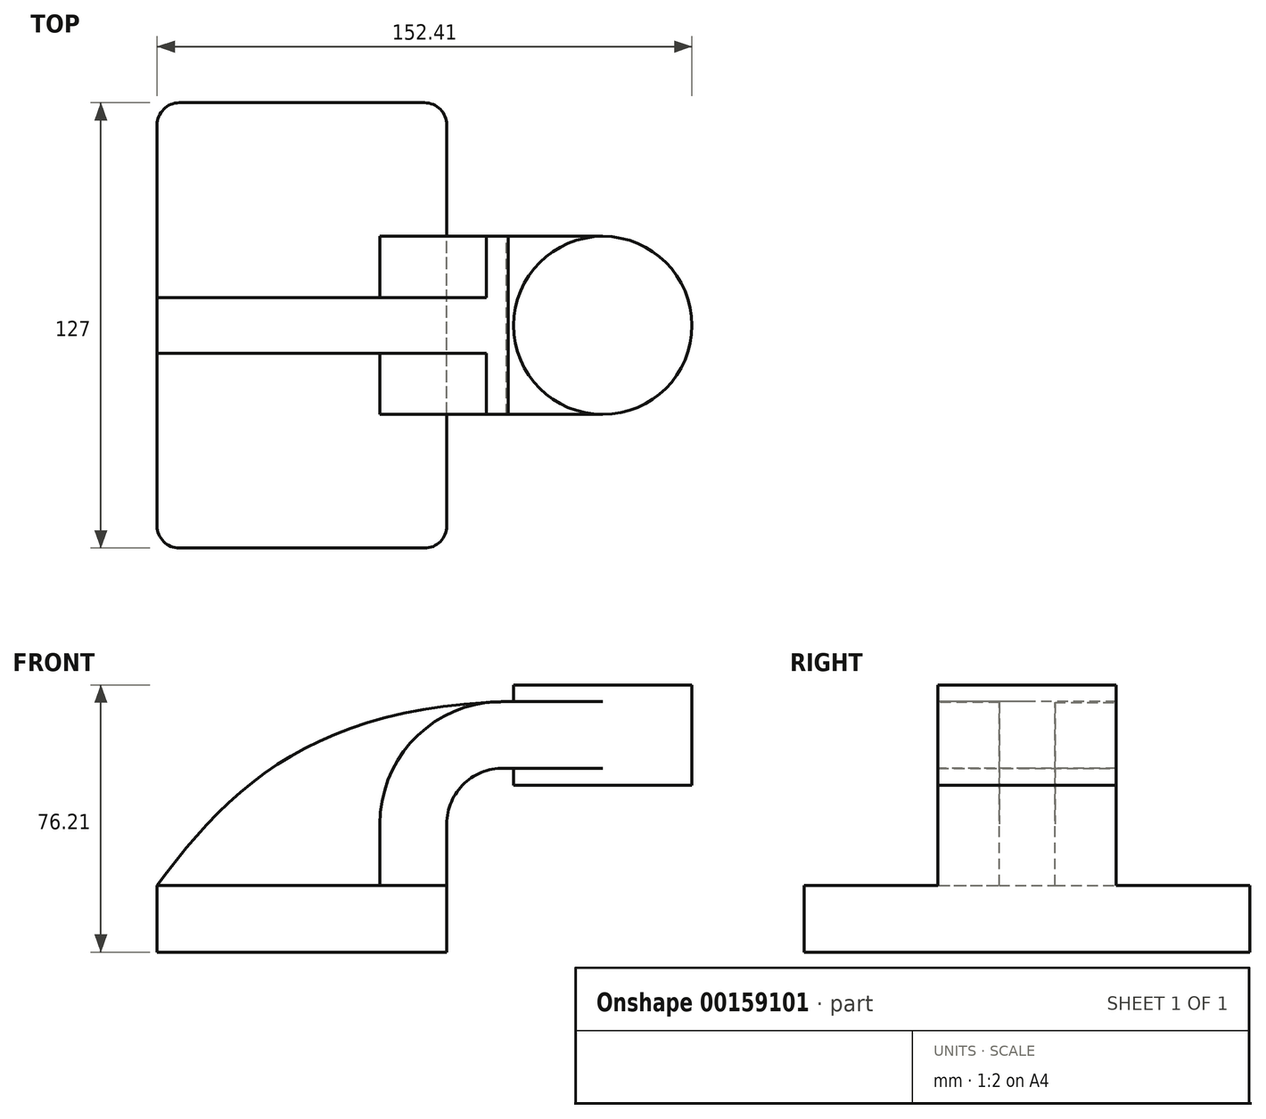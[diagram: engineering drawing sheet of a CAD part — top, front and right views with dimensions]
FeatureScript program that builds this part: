
annotation { "Feature Type Name" : "Feature", "Feature Type Description" : "" }
export const myFeature = defineFeature(function(context is Context, id is Id, definition is map)
    precondition{}
    {
        {
            var Q0;
            Q0=qCreatedBy(makeId("Front.planeOp"),FACE);
            var sketch = newSketch(context, id + "F0", { "sketchPlane" : qUnion([Q0])});
            skLineSegment(sketch, "E0.bottom", {"start": v(-41.28, 9.52) * mm, "end": v(41.28, 9.52) * mm});
            skLineSegment(sketch, "E0.top", {"start": v(-41.28, -9.52) * mm, "end": v(41.28, -9.52) * mm});
            skLineSegment(sketch, "E0.left", {"start": v(-41.28, 9.52) * mm, "end": v(-41.28, -9.52) * mm});
            skLineSegment(sketch, "E0.right", {"start": v(41.28, 9.52) * mm, "end": v(41.28, -9.52) * mm});
            skPoint(sketch, "E0.middle", {"position": v(0, 0) * mm});
            skLineSegment(sketch, "E1", {"start": v(41.28, 9.52) * mm, "end": v(41.28, 27.04) * mm});
            skArc(sketch, "E2", {"start": v(41.28, 27.04) * mm, "mid": v(46.32, 38.65) * mm, "end": v(58.25, 42.88) * mm});
            skLineSegment(sketch, "E3", {"start": v(58.25, 42.88) * mm, "end": v(85.73, 42.88) * mm});
            skLineSegment(sketch, "E4.bottom", {"start": v(111.12, 38.1) * mm, "end": v(60.33, 38.1) * mm});
            skLineSegment(sketch, "E4.top", {"start": v(111.12, 66.68) * mm, "end": v(60.33, 66.68) * mm});
            skLineSegment(sketch, "E4.left", {"start": v(111.13, 38.1) * mm, "end": v(111.13, 66.68) * mm});
            skLineSegment(sketch, "E4.right", {"start": v(60.33, 38.1) * mm, "end": v(60.33, 66.68) * mm});
            skPoint(sketch, "E4.middle", {"position": v(85.73, 52.39) * mm});
            skLineSegment(sketch, "E5.0", {"start": v(58.78, 61.93) * mm, "end": v(85.73, 61.93) * mm});
            skArc(sketch, "E5.1", {"start": v(22.23, 27.04) * mm, "mid": v(33.04, 52.3) * mm, "end": v(58.78, 61.93) * mm});
            skLineSegment(sketch, "E5.2", {"start": v(22.23, 9.52) * mm, "end": v(22.23, 27.04) * mm});
            skFitSpline(sketch, "E6", {"points": [v(-41.28, 9.52) * mm, v(58.78, 61.93) * mm], "startDerivative": vector(65.14, 88.62) * mm, "endDerivative": vector(161.42, 4.32) * mm});
            skLineSegment(sketch, "E7", {"start": v(85.73, 38.1) * mm, "end": v(85.73, 66.68) * mm});
            skSolve(sketch);
        }
        {
            var Q0;
            Q0=makeQuery(id+"F0.imprint","IMPRINT",FACE,{"disambiguationData":[TD([[makeQuery(id+"F0.imprint","IMPRINT",EDGE,{"derivedFrom":sQuery(id+"F0.wireOp",EDGE,"E0.top")}),1.0]])]});
            extrude(context, id + "F1", {"entities" : qUnion([Q0]), "endBound" : BoundingType.SYMMETRIC, "depth" : 127 * mm});
        }
        {
            var Q0;
            {var subQ10=sQuery(id+"F0.wireOp",EDGE,"E1");Q0=makeQuery(id+"F0.imprint","IMPRINT",FACE,{"disambiguationData":[TD([[makeQuery(id+"F0.imprint","IMPRINT",EDGE,{"derivedFrom":subQ10}),1.0]])]});}
            var Q1;
            {var subQ0=sQuery(id+"F0.wireOp",EDGE,"E7");var subQ1=sQuery(id+"F0.wireOp",EDGE,"E3");var subQ2=makeQuery(id+"F0.imprint","INTERSECT",VERTEX,{"derivedFrom":[subQ1,subQ0]});Q1=makeQuery(id+"F0.imprint","IMPRINT",FACE,{"disambiguationData":[TD([[makeQuery(id+"F0.imprint","IMPRINT",EDGE,{"disambiguationData":[TD([[subQ2,1.0]])],"derivedFrom":subQ1}),1.0]])]});}
            extrude(context, id + "F2", {"entities" : qUnion([Q0, Q1]), "operationType" : NewBodyOperationType.ADD, "endBound" : BoundingType.SYMMETRIC, "depth" : 50.8 * mm});
        }
        {
            var Q0;
            {var subQ3=sQuery(id+"F0.wireOp",EDGE,"E5.2");Q0=makeQuery(id+"F0.imprint","IMPRINT",FACE,{"disambiguationData":[TD([[makeQuery(id+"F0.imprint","IMPRINT",EDGE,{"derivedFrom":subQ3}),1.0]])]});}
            extrude(context, id + "F3", {"entities" : qUnion([Q0]), "operationType" : NewBodyOperationType.ADD, "endBound" : BoundingType.SYMMETRIC, "depth" : 15.88 * mm});
        }
        {
            var Q0;
            {var subQ0=sQuery(id+"F0.wireOp",EDGE,"E4.left");Q0=makeQuery(id+"F0.imprint","IMPRINT",FACE,{"disambiguationData":[TD([[makeQuery(id+"F0.imprint","IMPRINT",EDGE,{"derivedFrom":subQ0}),1.0]])]});}
            var Q1;
            Q1=sQuery(id+"F0.wireOp",EDGE,"E7");
            revolve(context, id + "F4", {"operationType" : NewBodyOperationType.ADD, "entities" : qUnion([Q0]), "axis" : qUnion([Q1]), "revolveType" : RevolveType.FULL});
        }
        {
            var Q0;
            Q0=makeQuery(id+"F1.opExtrude","CAP_EDGE",EDGE,{"disambiguationData":[OSD([sQuery(id+"F0.wireOp",EDGE,"E0.left")])],"isStart":false});
            var Q1;
            Q1=makeQuery(id+"F1.opExtrude","CAP_EDGE",EDGE,{"disambiguationData":[OSD([sQuery(id+"F0.wireOp",EDGE,"E0.right")])],"isStart":false});
            var Q2;
            Q2=makeQuery(id+"F1.opExtrude","CAP_EDGE",EDGE,{"disambiguationData":[OSD([sQuery(id+"F0.wireOp",EDGE,"E0.right")])],"isStart":true});
            var Q3;
            Q3=makeQuery(id+"F1.opExtrude","CAP_EDGE",EDGE,{"disambiguationData":[OSD([sQuery(id+"F0.wireOp",EDGE,"E0.left")])],"isStart":true});
            fillet(context, id + "F5", {"entities" : qUnion([Q0, Q1, Q2, Q3]), "radius" : 6.35 * mm, "tangentPropagation" : true, "allowEdgeOverflow" : false});
        }
    });
